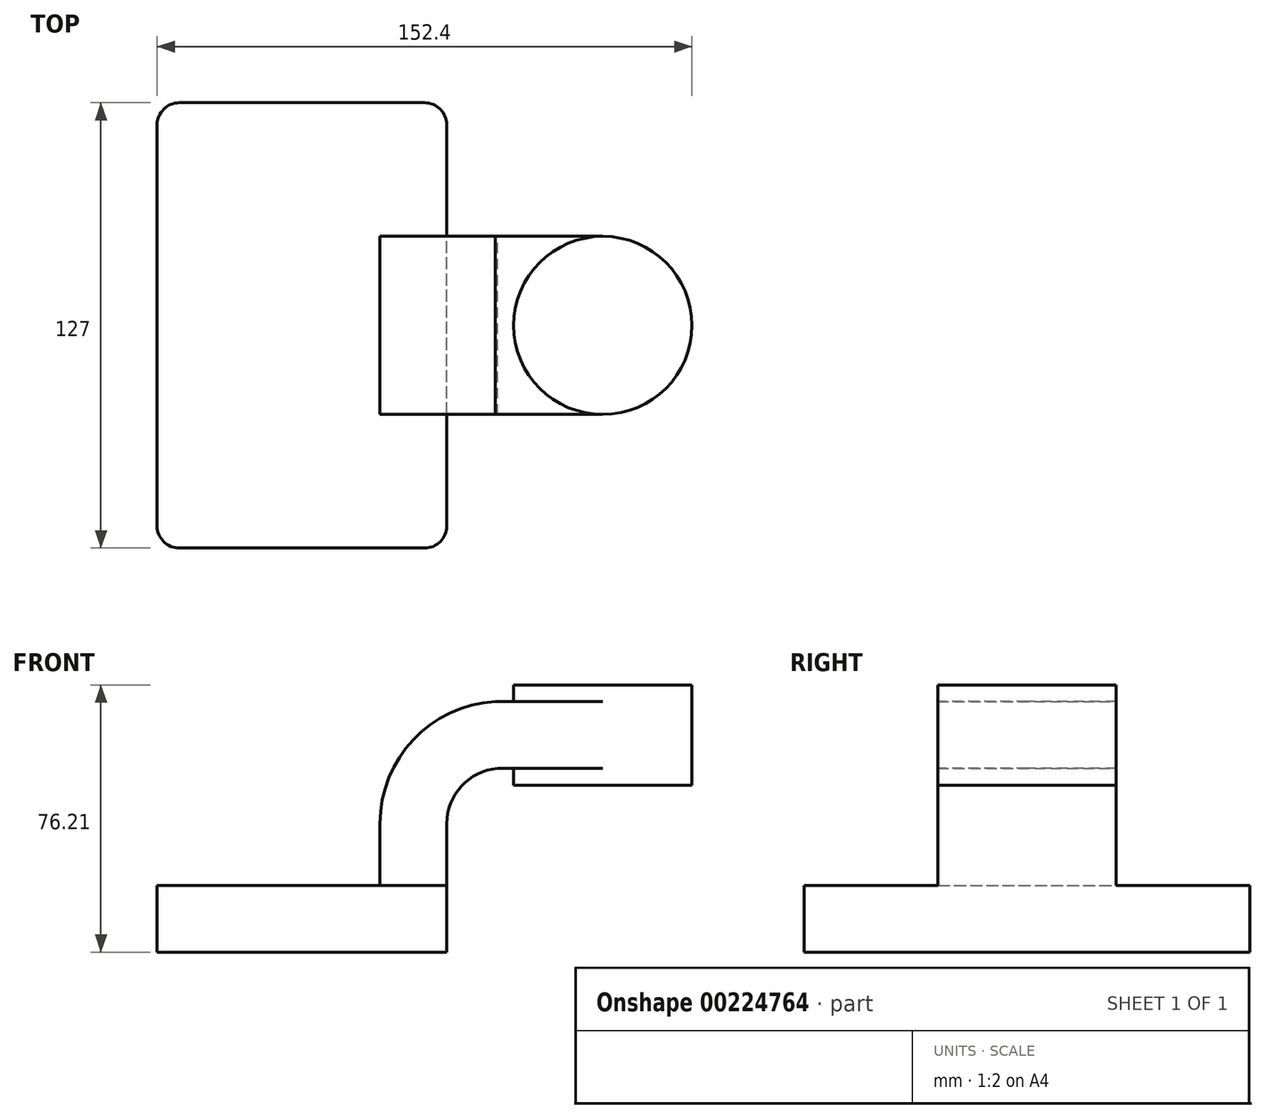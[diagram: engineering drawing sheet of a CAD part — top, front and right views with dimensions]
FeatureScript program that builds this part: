
annotation { "Feature Type Name" : "Feature", "Feature Type Description" : "" }
export const myFeature = defineFeature(function(context is Context, id is Id, definition is map)
    precondition{}
    {
        {
            var Q0;
            Q0=qCreatedBy(makeId("Front.planeOp"),FACE);
            var sketch = newSketch(context, id + "F0", { "sketchPlane" : qUnion([Q0])});
            skLineSegment(sketch, "E0.bottom", {"start": v(41.28, 9.53) * mm, "end": v(-41.28, 9.53) * mm});
            skLineSegment(sketch, "E0.top", {"start": v(41.28, -9.52) * mm, "end": v(-41.28, -9.52) * mm});
            skLineSegment(sketch, "E0.left", {"start": v(41.28, 9.53) * mm, "end": v(41.28, -9.52) * mm});
            skLineSegment(sketch, "E0.right", {"start": v(-41.28, 9.53) * mm, "end": v(-41.28, -9.52) * mm});
            skPoint(sketch, "E0.middle", {"position": v(0, 0) * mm});
            skLineSegment(sketch, "E1.bottom", {"start": v(60.33, 38.1) * mm, "end": v(111.13, 38.1) * mm});
            skLineSegment(sketch, "E1.top", {"start": v(60.33, 66.68) * mm, "end": v(111.13, 66.68) * mm});
            skLineSegment(sketch, "E1.left", {"start": v(60.33, 38.1) * mm, "end": v(60.32, 66.67) * mm});
            skLineSegment(sketch, "E1.right", {"start": v(111.13, 38.1) * mm, "end": v(111.13, 66.68) * mm});
            skPoint(sketch, "E1.middle", {"position": v(85.73, 52.39) * mm});
            skLineSegment(sketch, "E2", {"start": v(41.28, 9.53) * mm, "end": v(41.28, 27.06) * mm});
            skArc(sketch, "E3", {"start": v(41.27, 27.06) * mm, "mid": v(45.43, 37.78) * mm, "end": v(55.73, 42.88) * mm});
            skLineSegment(sketch, "E4", {"start": v(55.73, 42.88) * mm, "end": v(85.73, 42.88) * mm});
            skLineSegment(sketch, "E5.0", {"start": v(55.04, 61.93) * mm, "end": v(85.73, 61.93) * mm});
            skArc(sketch, "E5.1", {"start": v(22.22, 27.06) * mm, "mid": v(31.72, 51) * mm, "end": v(55.04, 61.93) * mm});
            skLineSegment(sketch, "E5.2", {"start": v(22.22, 9.53) * mm, "end": v(22.22, 27.06) * mm});
            skLineSegment(sketch, "E6", {"start": v(85.73, 38.1) * mm, "end": v(85.73, 66.68) * mm});
            skFitSpline(sketch, "E7", {"points": [v(-41.28, 9.52) * mm, v(55.04, 61.93) * mm], "startDerivative": vector(0, 75.83) * mm, "endDerivative": vector(116.39, 0) * mm});
            skSolve(sketch);
        }
        {
            var Q0;
            Q0=makeQuery(id+"F0.imprint","IMPRINT",FACE,{"disambiguationData":[TD([[makeQuery(id+"F0.imprint","IMPRINT",EDGE,{"derivedFrom":sQuery(id+"F0.wireOp",EDGE,"E0.top")}),-1.0]])]});
            extrude(context, id + "F1", {"entities" : qUnion([Q0]), "depth" : 127 * mm, "symmetric" : true});
        }
        {
            var Q0;
            {var subQ1=sQuery(id+"F0.wireOp",EDGE,"E2");Q0=makeQuery(id+"F0.imprint","IMPRINT",FACE,{"disambiguationData":[TD([[makeQuery(id+"F0.imprint","IMPRINT",EDGE,{"derivedFrom":subQ1}),1.0]])]});}
            var Q1;
            {var subQ0=sQuery(id+"F0.wireOp",EDGE,"E4");var subQ1=sQuery(id+"F0.wireOp",EDGE,"E1.left");var subQ2=makeQuery(id+"F0.imprint","INTERSECT",VERTEX,{"derivedFrom":[subQ1,subQ0]});Q1=makeQuery(id+"F0.imprint","IMPRINT",FACE,{"disambiguationData":[TD([[makeQuery(id+"F0.imprint","IMPRINT",EDGE,{"disambiguationData":[TD([[subQ2,-1.0]])],"derivedFrom":subQ1}),-1.0]])]});}
            extrude(context, id + "F2", {"entities" : qUnion([Q0, Q1]), "operationType" : NewBodyOperationType.ADD, "depth" : 50.8 * mm, "symmetric" : true});
        }
        {
            var Q0;
            Q0=makeQuery(id+"F0.imprint","IMPRINT",FACE,{"disambiguationData":[TD([[makeQuery(id+"F0.imprint","IMPRINT",EDGE,{"derivedFrom":sQuery(id+"F0.wireOp",EDGE,"E5.1")}),1.0]])]});
            extrude(context, id + "F3", {"entities" : qUnion([Q0]), "operationType" : NewBodyOperationType.ADD, "depth" : 15.88 * mm, "symmetric" : true});
        }
        {
            var Q0;
            {var subQ0=sQuery(id+"F0.wireOp",EDGE,"E1.right");Q0=makeQuery(id+"F0.imprint","IMPRINT",FACE,{"disambiguationData":[TD([[makeQuery(id+"F0.imprint","IMPRINT",EDGE,{"derivedFrom":subQ0}),1.0]])]});}
            var Q1;
            Q1=sQuery(id+"F0.wireOp",EDGE,"E6");
            revolve(context, id + "F4", {"operationType" : NewBodyOperationType.ADD, "entities" : qUnion([Q0]), "axis" : qUnion([Q1]), "revolveType" : RevolveType.FULL});
        }
        {
            var Q0;
            Q0=makeQuery(id+"F1.opExtrude","CAP_EDGE",EDGE,{"disambiguationData":[OSD([sQuery(id+"F0.wireOp",EDGE,"E0.right")])],"isStart":false});
            var Q1;
            Q1=makeQuery(id+"F1.opExtrude","CAP_EDGE",EDGE,{"disambiguationData":[OSD([sQuery(id+"F0.wireOp",EDGE,"E0.left")])],"isStart":false});
            var Q2;
            Q2=makeQuery(id+"F1.opExtrude","CAP_EDGE",EDGE,{"disambiguationData":[OSD([sQuery(id+"F0.wireOp",EDGE,"E0.left")])],"isStart":true});
            var Q3;
            Q3=makeQuery(id+"F1.opExtrude","CAP_EDGE",EDGE,{"disambiguationData":[OSD([sQuery(id+"F0.wireOp",EDGE,"E0.right")])],"isStart":true});
            fillet(context, id + "F5", {"entities" : qUnion([Q0, Q1, Q2, Q3]), "radius" : 6.35 * mm, "tangentPropagation" : true, "allowEdgeOverflow" : false});
        }
    });
